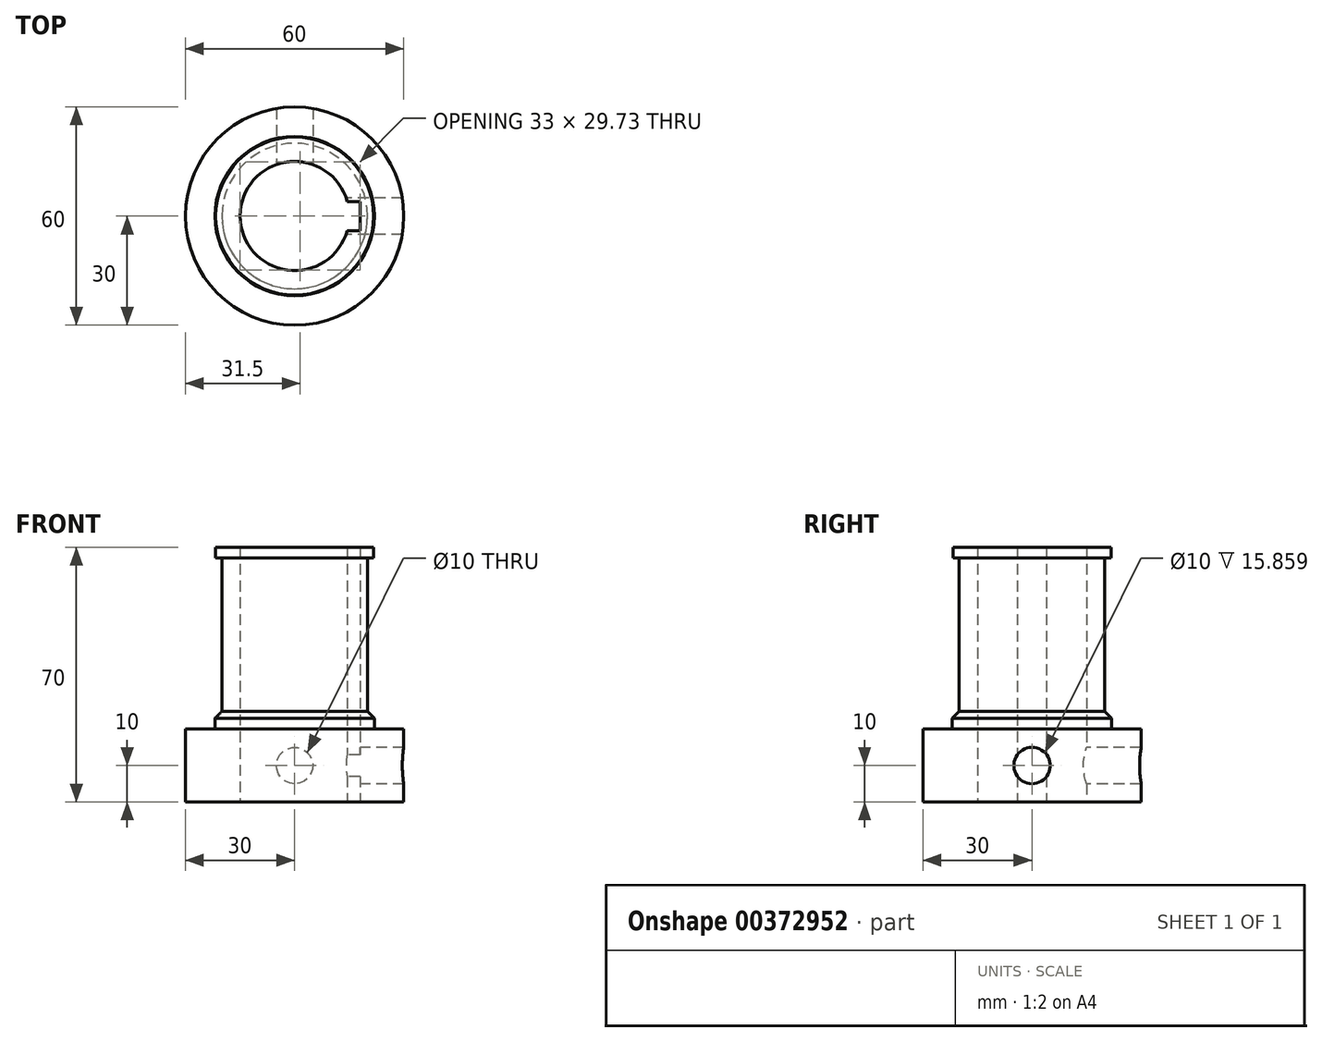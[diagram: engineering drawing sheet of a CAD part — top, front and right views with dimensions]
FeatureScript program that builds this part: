
annotation { "Feature Type Name" : "Feature", "Feature Type Description" : "" }
export const myFeature = defineFeature(function(context is Context, id is Id, definition is map)
    precondition{}
    {
        {
            var Q0;
            Q0=qCreatedBy(makeId("Top.planeOp"),FACE);
            var sketch = newSketch(context, id + "F0", { "sketchPlane" : qUnion([Q0])});
            skCircle(sketch, "E0", {"center": v(0, 0) * mm, "radius": 30 * mm});
            skArc(sketch, "E1", {"start": v(14.46, 4) * mm, "mid": v(-15, 0) * mm, "end": v(14.46, -4) * mm});
            skLineSegment(sketch, "E2", {"start": v(18, 0) * mm, "end": v(18, -4) * mm});
            skLineSegment(sketch, "E3", {"start": v(18, -4) * mm, "end": v(14.46, -4) * mm});
            skLineSegment(sketch, "E4", {"start": v(18, 0) * mm, "end": v(18, 4) * mm});
            skLineSegment(sketch, "E5", {"start": v(18, 4) * mm, "end": v(14.46, 4) * mm});
            skPoint(sketch, "E6.orphan", {"position": v(15, 0) * mm});
            skSolve(sketch);
        }
        {
            var Q0;
            Q0=makeQuery(id+"F0.imprint","IMPRINT",FACE,{"disambiguationData":[TD([[makeQuery(id+"F0.imprint","IMPRINT",EDGE,{"derivedFrom":sQuery(id+"F0.wireOp",EDGE,"E0")}),1.0]])]});
            extrude(context, id + "F1", {"entities" : qUnion([Q0]), "depth" : 20 * mm});
        }
        {
            var Q0;
            Q0=makeQuery(id+"F1.opExtrude","CAP_FACE",FACE,{"disambiguationData":[OSD([sQuery(id+"F0.wireOp",EDGE,"E0"),sQuery(id+"F0.wireOp",EDGE,"E1"),sQuery(id+"F0.wireOp",EDGE,"E2"),sQuery(id+"F0.wireOp",EDGE,"E3"),sQuery(id+"F0.wireOp",EDGE,"E4"),sQuery(id+"F0.wireOp",EDGE,"E5")])],"isStart":false});
            var sketch = newSketch(context, id + "F2", { "sketchPlane" : qUnion([Q0])});
            skArc(sketch, "E7", {"start": v(14.46, 4) * mm, "mid": v(-15, 0) * mm, "end": v(14.46, -4) * mm});
            skLineSegment(sketch, "E8", {"start": v(18, -4) * mm, "end": v(18, 4) * mm});
            skLineSegment(sketch, "E9", {"start": v(18, 4) * mm, "end": v(14.46, 4) * mm});
            skLineSegment(sketch, "E10", {"start": v(18, -4) * mm, "end": v(14.46, -4) * mm});
            skCircle(sketch, "E11", {"center": v(0, 0) * mm, "radius": 21.9 * mm});
            skSolve(sketch);
        }
        {
            var Q0;
            Q0=makeQuery(id+"F2.imprint","IMPRINT",FACE,{"disambiguationData":[TD([[makeQuery(id+"F2.imprint","IMPRINT",EDGE,{"derivedFrom":sQuery(id+"F2.wireOp",EDGE,"E7")}),-1.0]])]});
            extrude(context, id + "F3", {"entities" : qUnion([Q0]), "operationType" : NewBodyOperationType.ADD, "depth" : 5 * mm});
        }
        {
            var Q0;
            Q0=makeQuery(id+"F3.opExtrude","CAP_FACE",FACE,{"disambiguationData":[OSD([sQuery(id+"F2.wireOp",EDGE,"E7"),sQuery(id+"F2.wireOp",EDGE,"E8"),sQuery(id+"F2.wireOp",EDGE,"E9"),sQuery(id+"F2.wireOp",EDGE,"E10"),sQuery(id+"F2.wireOp",EDGE,"E11")])],"isStart":false});
            var sketch = newSketch(context, id + "F4", { "sketchPlane" : qUnion([Q0])});
            skArc(sketch, "E12", {"start": v(14.46, 4) * mm, "mid": v(-15, 0) * mm, "end": v(14.46, -4) * mm});
            skCircle(sketch, "E13", {"center": v(0, 0) * mm, "radius": 20 * mm});
            skLineSegment(sketch, "E14", {"start": v(14.46, -4) * mm, "end": v(18, -4) * mm});
            skLineSegment(sketch, "E15", {"start": v(18, -4) * mm, "end": v(18, 4) * mm});
            skLineSegment(sketch, "E16", {"start": v(18, 4) * mm, "end": v(14.46, 4) * mm});
            skSolve(sketch);
        }
        {
            var Q0;
            Q0=makeQuery(id+"F4.imprint","IMPRINT",FACE,{"disambiguationData":[TD([[makeQuery(id+"F4.imprint","IMPRINT",EDGE,{"derivedFrom":sQuery(id+"F4.wireOp",EDGE,"E12")}),-1.0]])]});
            extrude(context, id + "F5", {"entities" : qUnion([Q0]), "operationType" : NewBodyOperationType.ADD, "depth" : 42 * mm});
        }
        {
            var Q0;
            Q0=makeQuery(id+"F5.opExtrude","CAP_FACE",FACE,{"disambiguationData":[OSD([sQuery(id+"F4.wireOp",EDGE,"E12"),sQuery(id+"F4.wireOp",EDGE,"E13"),sQuery(id+"F4.wireOp",EDGE,"E14"),sQuery(id+"F4.wireOp",EDGE,"E15"),sQuery(id+"F4.wireOp",EDGE,"E16")])],"isStart":false});
            var sketch = newSketch(context, id + "F6", { "sketchPlane" : qUnion([Q0])});
            skArc(sketch, "E17", {"start": v(14.46, 4) * mm, "mid": v(-15, 0) * mm, "end": v(14.46, -4) * mm});
            skCircle(sketch, "E18", {"center": v(0, 0) * mm, "radius": 21.7 * mm});
            skLineSegment(sketch, "E19", {"start": v(14.46, -4) * mm, "end": v(18, -4) * mm});
            skLineSegment(sketch, "E20", {"start": v(18, -4) * mm, "end": v(18, 4) * mm});
            skLineSegment(sketch, "E21", {"start": v(18, 4) * mm, "end": v(14.46, 4) * mm});
            skSolve(sketch);
        }
        {
            var Q0;
            Q0=makeQuery(id+"F6.imprint","IMPRINT",FACE,{"disambiguationData":[TD([[makeQuery(id+"F6.imprint","IMPRINT",EDGE,{"derivedFrom":sQuery(id+"F6.wireOp",EDGE,"E17")}),-1.0]])]});
            var Q1;
            Q1=makeQuery(id+"F6.imprint","IMPRINT",FACE,{"disambiguationData":[TD([[makeQuery(id+"F6.imprint","IMPRINT",EDGE,{"derivedFrom":sQuery(id+"F6.wireOp",EDGE,"E18")}),1.0]])]});
            extrude(context, id + "F7", {"entities" : qUnion([Q0, Q1]), "operationType" : NewBodyOperationType.ADD, "depth" : 3 * mm});
        }
        {
            var Q0;
            Q0=qCreatedBy(makeId("Right.planeOp"),FACE);
            var sketch = newSketch(context, id + "F8", { "sketchPlane" : qUnion([Q0])});
            skLineSegment(sketch, "E22", {"start": v(0, 0) * mm, "end": v(0, 10) * mm});
            skCircle(sketch, "E23", {"center": v(0, 10) * mm, "radius": 4 * mm});
            skSolve(sketch);
        }
        {
            var Q0;
            Q0=sQuery(id+"F8.wireOp",VERTEX,"E23.center");
            var Q1;
            Q1=makeQuery(id+"F1.opExtrude","SWEPT_BODY",BODY,{"disambiguationData":[OSD([sQuery(id+"F0.wireOp",EDGE,"E0"),sQuery(id+"F0.wireOp",EDGE,"E1"),sQuery(id+"F0.wireOp",EDGE,"E2"),sQuery(id+"F0.wireOp",EDGE,"E3"),sQuery(id+"F0.wireOp",EDGE,"E4"),sQuery(id+"F0.wireOp",EDGE,"E5")])]});
            hole(context, id + "F9", {"style" : HoleStyle.SIMPLE, "endStyle" : HoleEndStyle.BLIND, "oppositeDirection" : true, "holeDiameter" : 10 * mm, "holeDepth" : 80 * mm, "isTappedThrough" : true, "tappedDepth" : 12 * mm, "tapClearance" : 3, "startFromSketch" : true, "locations" : qUnion([Q0]), "scope" : qUnion([Q1])});
        }
        {
            var Q0;
            Q0=qCreatedBy(makeId("Front.planeOp"),FACE);
            var sketch = newSketch(context, id + "F10", { "sketchPlane" : qUnion([Q0])});
            skLineSegment(sketch, "E24", {"start": v(0, 0) * mm, "end": v(0, 10) * mm});
            skSolve(sketch);
        }
        {
            var Q0;
            Q0=sQuery(id+"F10.wireOp",VERTEX,"E24.end");
            var Q1;
            Q1=makeQuery(id+"F1.opExtrude","SWEPT_BODY",BODY,{"disambiguationData":[OSD([sQuery(id+"F0.wireOp",EDGE,"E0"),sQuery(id+"F0.wireOp",EDGE,"E1"),sQuery(id+"F0.wireOp",EDGE,"E2"),sQuery(id+"F0.wireOp",EDGE,"E3"),sQuery(id+"F0.wireOp",EDGE,"E4"),sQuery(id+"F0.wireOp",EDGE,"E5")])]});
            hole(context, id + "F11", {"style" : HoleStyle.SIMPLE, "endStyle" : HoleEndStyle.BLIND, "holeDiameter" : 10 * mm, "holeDepth" : 50 * mm, "isTappedThrough" : true, "tappedDepth" : 12 * mm, "tapClearance" : 3, "startFromSketch" : true, "locations" : qUnion([Q0]), "scope" : qUnion([Q1])});
        }
        {
            var Q0;
            Q0=makeQuery(id+"F3.opExtrude","CAP_EDGE",EDGE,{"disambiguationData":[OSD([sQuery(id+"F2.wireOp",EDGE,"E11")])],"isStart":false});
            chamfer(context, id + "F12", {"entities" : qUnion([Q0]), "width" : 2 * mm, "tangentPropagation" : true});
        }
    });
